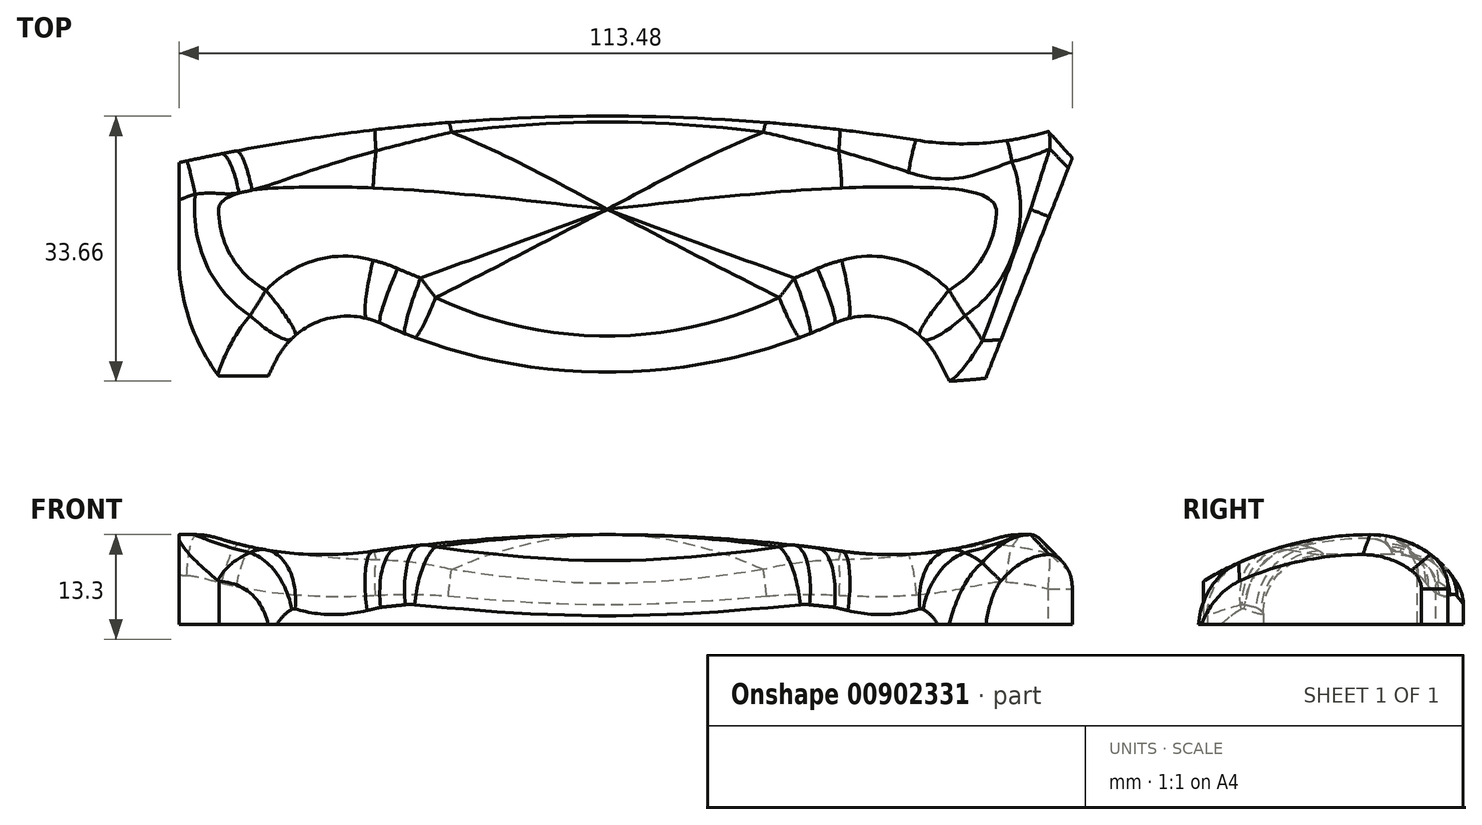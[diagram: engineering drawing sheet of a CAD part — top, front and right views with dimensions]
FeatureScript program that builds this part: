
annotation { "Feature Type Name" : "Feature", "Feature Type Description" : "" }
export const myFeature = defineFeature(function(context is Context, id is Id, definition is map)
    precondition{}
    {
        {
            var Q0;
            Q0=qCreatedBy(makeId("Top.planeOp"),FACE);
            var sketch = newSketch(context, id + "F0", { "sketchPlane" : qUnion([Q0])});
            skLineSegment(sketch, "E0", {"start": v(0, 35.56) * mm, "end": v(0, 0) * mm, "construction": true});
            skLineSegment(sketch, "E1", {"start": v(0, 0) * mm, "end": v(101.6, 0) * mm, "construction": true});
            skLineSegment(sketch, "E2", {"start": v(101.6, 0) * mm, "end": v(115.57, 35.56) * mm, "construction": true});
            skLineSegment(sketch, "E3", {"start": v(115.57, 35.56) * mm, "end": v(0, 35.56) * mm, "construction": true});
            skSolve(sketch);
        }
        {
            var Q0;
            Q0=qCreatedBy(makeId("Top.planeOp"),FACE);
            var sketch = newSketch(context, id + "F1", { "sketchPlane" : qUnion([Q0])});
            skLineSegment(sketch, "E4.0", {"start": v(115.57, 35.56) * mm, "end": v(0, 35.56) * mm, "construction": true});
            skLineSegment(sketch, "E5.0", {"start": v(0, 35.56) * mm, "end": v(0, 0) * mm, "construction": true});
            skLineSegment(sketch, "E6.0", {"start": v(0, 0) * mm, "end": v(101.6, 0) * mm, "construction": true});
            skLineSegment(sketch, "E7.0", {"start": v(101.6, 0) * mm, "end": v(115.57, 35.56) * mm, "construction": true});
            skArc(sketch, "E8", {"start": v(112.9, 28.74) * mm, "mid": v(103.33, 30.8) * mm, "end": v(93.7, 32.5) * mm, "construction": true});
            skArc(sketch, "E9", {"start": v(0, 17.78) * mm, "mid": v(1.89, 8.18) * mm, "end": v(7.26, 0) * mm});
            skLineSegment(sketch, "E10", {"start": v(0, 29.66) * mm, "end": v(0, 17.78) * mm});
            skArc(sketch, "E11", {"start": v(93.7, 32.5) * mm, "mid": v(104.86, 32.41) * mm, "end": v(115.57, 35.56) * mm});
            skArc(sketch, "E12", {"start": v(25.6, 9.25) * mm, "mid": v(15.9, 8.54) * mm, "end": v(11.25, 0) * mm});
            skArc(sketch, "E13", {"start": v(25.6, 9.25) * mm, "mid": v(54.43, 3.03) * mm, "end": v(83.26, 9.25) * mm});
            skArc(sketch, "E14", {"start": v(93.7, 32.5) * mm, "mid": v(46.72, 35.44) * mm, "end": v(0, 29.66) * mm});
            skLineSegment(sketch, "E15", {"start": v(115.57, 35.56) * mm, "end": v(101.6, 0) * mm});
            skLineSegment(sketch, "E16", {"start": v(97.61, 0) * mm, "end": v(101.6, 0) * mm});
            skArc(sketch, "E17", {"start": v(97.61, 0) * mm, "mid": v(92.96, 8.54) * mm, "end": v(83.26, 9.25) * mm});
            skLineSegment(sketch, "E18", {"start": v(7.26, 0) * mm, "end": v(11.25, 0) * mm});
            skLineSegment(sketch, "E19", {"start": v(54.43, -218.44) * mm, "end": v(54.43, 72.88) * mm, "construction": true});
            skSolve(sketch);
        }
        {
            var Q0;
            Q0=qSketchRegion(id+"F1",true);
            extrude(context, id + "F2", {"entities" : qUnion([Q0]), "depth" : 19.05 * mm, "offsetDistance" : 25.4 * mm});
        }
        {
            var Q0;
            Q0=qCreatedBy(makeId("Right.planeOp"),FACE);
            var sketch = newSketch(context, id + "F3", { "sketchPlane" : qUnion([Q0])});
            skLineSegment(sketch, "E20.0", {"start": v(35.56, 0) * mm, "end": v(0, 0) * mm, "construction": true});
            skLineSegment(sketch, "E21", {"start": v(35.56, 0) * mm, "end": v(35.56, 3.8) * mm, "construction": true});
            skLineSegment(sketch, "E22", {"start": v(35.56, 3.8) * mm, "end": v(35.56, 3.8) * mm});
            skLineSegment(sketch, "E23", {"start": v(0, 3.8) * mm, "end": v(0, 0) * mm, "construction": true});
            skLineSegment(sketch, "E24", {"start": v(23.72, 19.05) * mm, "end": v(23.72, -1.58) * mm, "construction": true});
            skLineSegment(sketch, "E25", {"start": v(17.78, 19.05) * mm, "end": v(17.78, -15.36) * mm, "construction": true});
            skArc(sketch, "E26", {"start": v(23.72, 11.43) * mm, "mid": v(11.26, 9.48) * mm, "end": v(0, 3.8) * mm});
            skArc(sketch, "E27", {"start": v(0, 3.8) * mm, "mid": v(36.18, -68.07) * mm, "end": v(23.72, 11.43) * mm, "construction": true});
            skLineSegment(sketch, "E28", {"start": v(35.56, 3.8) * mm, "end": v(0, 3.8) * mm, "construction": true});
            skArc(sketch, "E29", {"start": v(23.72, 11.43) * mm, "mid": v(16.68, -12.52) * mm, "end": v(35.56, 3.8) * mm, "construction": true});
            skArc(sketch, "E30", {"start": v(35.56, 3.8) * mm, "mid": v(30.76, 9.36) * mm, "end": v(23.72, 11.43) * mm});
            skLineSegment(sketch, "E31.0", {"start": v(35.56, 19.05) * mm, "end": v(0, 19.05) * mm});
            skLineSegment(sketch, "E32", {"start": v(35.56, 3.8) * mm, "end": v(35.56, 19.05) * mm});
            skLineSegment(sketch, "E33", {"start": v(0, 19.05) * mm, "end": v(0, 3.8) * mm});
            skSolve(sketch);
        }
        {
            var Q0;
            Q0=qSketchRegion(id+"F3",true);
            extrude(context, id + "F4", {"entities" : qUnion([Q0]), "operationType" : NewBodyOperationType.REMOVE, "endBound" : BoundingType.THROUGH_ALL, "depth" : 254 * mm, "offsetDistance" : 25.4 * mm});
        }
        {
            var Q0;
            Q0=qCreatedBy(makeId("Front.planeOp"),FACE);
            var sketch = newSketch(context, id + "F5", { "sketchPlane" : qUnion([Q0])});
            skLineSegment(sketch, "E34.0", {"start": v(25.6, 0) * mm, "end": v(11.25, 0) * mm, "construction": true});
            skLineSegment(sketch, "E35.0", {"start": v(97.61, 0) * mm, "end": v(83.26, 0) * mm, "construction": true});
            skLineSegment(sketch, "E36", {"start": v(18.43, 53.34) * mm, "end": v(18.43, 0) * mm, "construction": true});
            skLineSegment(sketch, "E37", {"start": v(90.43, 0) * mm, "end": v(90.43, 53.34) * mm, "construction": true});
            skArc(sketch, "E38", {"start": v(84.2, 9.33) * mm, "mid": v(54.43, 11.43) * mm, "end": v(24.67, 9.33) * mm});
            skArc(sketch, "E39", {"start": v(24.67, 9.33) * mm, "mid": v(54.43, -412.55) * mm, "end": v(84.2, 9.33) * mm, "construction": true});
            skLineSegment(sketch, "E40", {"start": v(105.24, 11.43) * mm, "end": v(3.62, 11.43) * mm});
            skArc(sketch, "E41", {"start": v(3.62, 11.43) * mm, "mid": v(14.02, 9.1) * mm, "end": v(24.67, 9.33) * mm});
            skArc(sketch, "E42", {"start": v(24.67, 9.33) * mm, "mid": v(22.84, 97.57) * mm, "end": v(3.62, 11.43) * mm, "construction": true});
            skArc(sketch, "E43", {"start": v(105.24, 11.43) * mm, "mid": v(86.02, 97.57) * mm, "end": v(84.2, 9.33) * mm, "construction": true});
            skArc(sketch, "E44", {"start": v(84.2, 9.33) * mm, "mid": v(94.85, 9.1) * mm, "end": v(105.24, 11.43) * mm});
            skPoint(sketch, "E45.orphan", {"position": v(110.92, 11.43) * mm});
            skLineSegment(sketch, "E46", {"start": v(18.43, 11.43) * mm, "end": v(18.43, 8.89) * mm, "construction": true});
            skSolve(sketch);
        }
        {
            var Q0;
            Q0=qSketchRegion(id+"F5",true);
            extrude(context, id + "F6", {"entities" : qUnion([Q0]), "operationType" : NewBodyOperationType.REMOVE, "endBound" : BoundingType.THROUGH_ALL, "oppositeDirection" : true, "depth" : 101.6 * mm, "offsetDistance" : 25.4 * mm});
        }
        {
            var Q0;
            {var subQ0=sQuery(id+"F5.wireOp",EDGE,"E38");Q0=makeQuery(id+"F6.boolean.opBoolean","INTERSECT",EDGE,{"derivedFrom":[makeQuery(id+"F4.boolean.opBoolean","COPY",FACE,{"derivedFrom":makeQuery(id+"F4.opExtrude","SWEPT_FACE",FACE,{"disambiguationData":[OSD([sQuery(id+"F3.wireOp",EDGE,"E30")])]})}),makeQuery(id+"F6.opExtrude","SWEPT_FACE",FACE,{"disambiguationData":[OSD([subQ0]),TDD([makeQuery(id+"F5.imprint","IMPRINT",EDGE,{"disambiguationData":[TD([[makeQuery(id+"F5.imprint","INTERSECT",VERTEX,{"derivedFrom":[subQ0,sQuery(id+"F5.wireOp",EDGE,"E41")]}),1.0]])],"derivedFrom":subQ0})])]})]});}
            var Q1;
            {var subQ0=sQuery(id+"F5.wireOp",EDGE,"E38");Q1=makeQuery(id+"F6.boolean.opBoolean","INTERSECT",EDGE,{"derivedFrom":[makeQuery(id+"F4.boolean.opBoolean","COPY",FACE,{"derivedFrom":makeQuery(id+"F4.opExtrude","SWEPT_FACE",FACE,{"disambiguationData":[OSD([sQuery(id+"F3.wireOp",EDGE,"E30")])]})}),makeQuery(id+"F6.opExtrude","SWEPT_FACE",FACE,{"disambiguationData":[OSD([subQ0]),TDD([makeQuery(id+"F5.imprint","IMPRINT",EDGE,{"disambiguationData":[TD([[makeQuery(id+"F5.imprint","INTERSECT",VERTEX,{"derivedFrom":[subQ0,sQuery(id+"F5.wireOp",EDGE,"E44")]}),-1.0]])],"derivedFrom":subQ0})])]})]});}
            var Q2;
            {var subQ0=sQuery(id+"F5.wireOp",EDGE,"E38");Q2=makeQuery(id+"F6.boolean.opBoolean","INTERSECT",EDGE,{"derivedFrom":[makeQuery(id+"F4.boolean.opBoolean","COPY",FACE,{"derivedFrom":makeQuery(id+"F4.opExtrude","SWEPT_FACE",FACE,{"disambiguationData":[OSD([sQuery(id+"F3.wireOp",EDGE,"E26")])]})}),makeQuery(id+"F6.opExtrude","SWEPT_FACE",FACE,{"disambiguationData":[OSD([subQ0]),TDD([makeQuery(id+"F5.imprint","IMPRINT",EDGE,{"disambiguationData":[TD([[makeQuery(id+"F5.imprint","INTERSECT",VERTEX,{"derivedFrom":[subQ0,sQuery(id+"F5.wireOp",EDGE,"E44")]}),-1.0]])],"derivedFrom":subQ0})])]})]});}
            var Q3;
            {var subQ0=sQuery(id+"F5.wireOp",EDGE,"E38");Q3=makeQuery(id+"F6.boolean.opBoolean","INTERSECT",EDGE,{"derivedFrom":[makeQuery(id+"F4.boolean.opBoolean","COPY",FACE,{"derivedFrom":makeQuery(id+"F4.opExtrude","SWEPT_FACE",FACE,{"disambiguationData":[OSD([sQuery(id+"F3.wireOp",EDGE,"E26")])]})}),makeQuery(id+"F6.opExtrude","SWEPT_FACE",FACE,{"disambiguationData":[OSD([subQ0]),TDD([makeQuery(id+"F5.imprint","IMPRINT",EDGE,{"disambiguationData":[TD([[makeQuery(id+"F5.imprint","INTERSECT",VERTEX,{"derivedFrom":[subQ0,sQuery(id+"F5.wireOp",EDGE,"E41")]}),1.0]])],"derivedFrom":subQ0})])]})]});}
            fillet(context, id + "F7", {"entities" : qUnion([Q0, Q1, Q2, Q3]), "radius" : 10.16 * mm, "tangentPropagation" : true, "allowEdgeOverflow" : false});
        }
        {
            var Q0;
            Q0=makeQuery(id+"F4.boolean.opBoolean","INTERSECT",EDGE,{"derivedFrom":[makeQuery(id+"F2.opExtrude","SWEPT_FACE",FACE,{"disambiguationData":[OSD([sQuery(id+"F1.wireOp",EDGE,"E14")])]}),makeQuery(id+"F4.opExtrude","SWEPT_FACE",FACE,{"disambiguationData":[OSD([sQuery(id+"F3.wireOp",EDGE,"E30")])]})]});
            fillet(context, id + "F8", {"entities" : qUnion([Q0]), "radius" : 5.08 * mm, "tangentPropagation" : true, "allowEdgeOverflow" : false});
        }
        {
            var Q0;
            Q0=makeQuery(id+"F4.boolean.opBoolean","INTERSECT",EDGE,{"derivedFrom":[makeQuery(id+"F2.opExtrude","SWEPT_FACE",FACE,{"disambiguationData":[OSD([sQuery(id+"F1.wireOp",EDGE,"E13")])]}),makeQuery(id+"F4.opExtrude","SWEPT_FACE",FACE,{"disambiguationData":[OSD([sQuery(id+"F3.wireOp",EDGE,"E26")])]})]});
            fillet(context, id + "F9", {"entities" : qUnion([Q0]), "radius" : 7.62 * mm, "tangentPropagation" : true, "allowEdgeOverflow" : false});
        }
        {
            var Q0;
            Q0=makeQuery(id+"F4.boolean.opBoolean","INTERSECT",EDGE,{"derivedFrom":[makeQuery(id+"F2.opExtrude","SWEPT_FACE",FACE,{"disambiguationData":[OSD([sQuery(id+"F1.wireOp",EDGE,"E15")])]}),makeQuery(id+"F4.opExtrude","SWEPT_FACE",FACE,{"disambiguationData":[OSD([sQuery(id+"F3.wireOp",EDGE,"E30")])]})]});
            chamfer(context, id + "F10", {"entities" : qUnion([Q0]), "width" : 2.54 * mm, "tangentPropagation" : true});
        }
        {
            var Q0;
            Q0=qCreatedBy(makeId("Front.planeOp"),FACE);
            var sketch = newSketch(context, id + "F11", { "sketchPlane" : qUnion([Q0])});
            skLineSegment(sketch, "E47.bottom", {"start": v(0, 25.4) * mm, "end": v(25.4, 25.4) * mm});
            skLineSegment(sketch, "E47.top", {"start": v(0, 0) * mm, "end": v(25.4, 0) * mm});
            skLineSegment(sketch, "E47.left", {"start": v(0, 25.4) * mm, "end": v(0, 0) * mm});
            skLineSegment(sketch, "E47.right", {"start": v(25.4, 25.4) * mm, "end": v(25.4, 0) * mm});
            skSolve(sketch);
        }
        {
            var Q0;
            Q0 = qSketchRegion(id + "F11", true);
            extrude(context, id + "F12", {"entities" : qUnion([Q0]), "operationType" : NewBodyOperationType.REMOVE, "oppositeDirection" : true, "depth" : 2.54 * mm, "offsetDistance" : 25.4 * mm});
        }
    });
